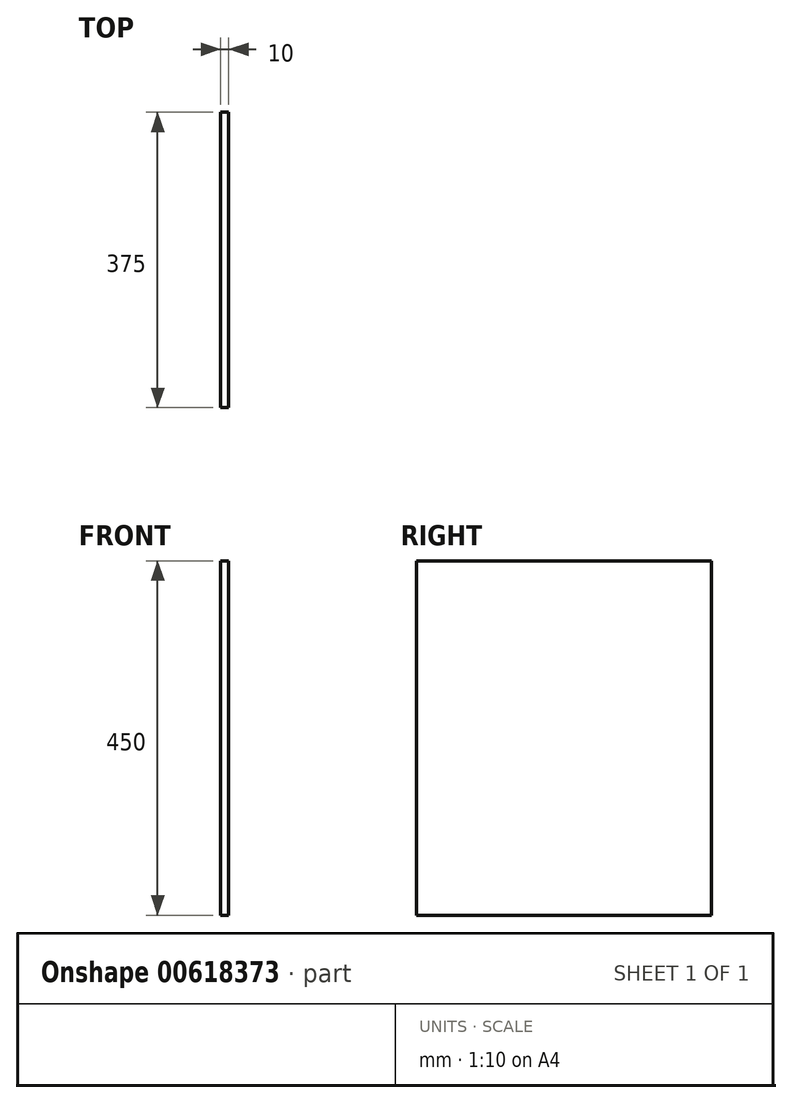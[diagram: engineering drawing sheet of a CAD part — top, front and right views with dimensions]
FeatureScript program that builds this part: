
annotation { "Feature Type Name" : "Feature", "Feature Type Description" : "" }
export const myFeature = defineFeature(function(context is Context, id is Id, definition is map)
    precondition{}
    {
        {
            var Q0;
            Q0=qCreatedBy(makeId("Right.planeOp"),FACE);
            var sketch = newSketch(context, id + "F0", { "sketchPlane" : qUnion([Q0])});
            skLineSegment(sketch, "E0.bottom", {"start": v(187.5, -225) * mm, "end": v(-187.5, -225) * mm});
            skLineSegment(sketch, "E0.top", {"start": v(187.5, 225) * mm, "end": v(-187.5, 225) * mm});
            skLineSegment(sketch, "E0.left", {"start": v(187.5, -225) * mm, "end": v(187.5, 225) * mm});
            skLineSegment(sketch, "E0.right", {"start": v(-187.5, -225) * mm, "end": v(-187.5, 225) * mm});
            skPoint(sketch, "E0.middle", {"position": v(0, 0) * mm});
            skSolve(sketch);
        }
        {
            var Q0;
            Q0=makeQuery(id+"F0.imprint","IMPRINT",FACE,{"disambiguationData":[TD([[makeQuery(id+"F0.imprint","IMPRINT",EDGE,{"derivedFrom":sQuery(id+"F0.wireOp",EDGE,"E0.bottom")}),-1.0]])]});
            extrude(context, id + "F1", {"entities" : qUnion([Q0]), "depth" : 5 * mm, "offsetDistance" : 25 * mm, "hasSecondDirection" : true, "secondDirectionOppositeDirection" : true, "secondDirectionDepth" : 5 * mm});
        }
    });
